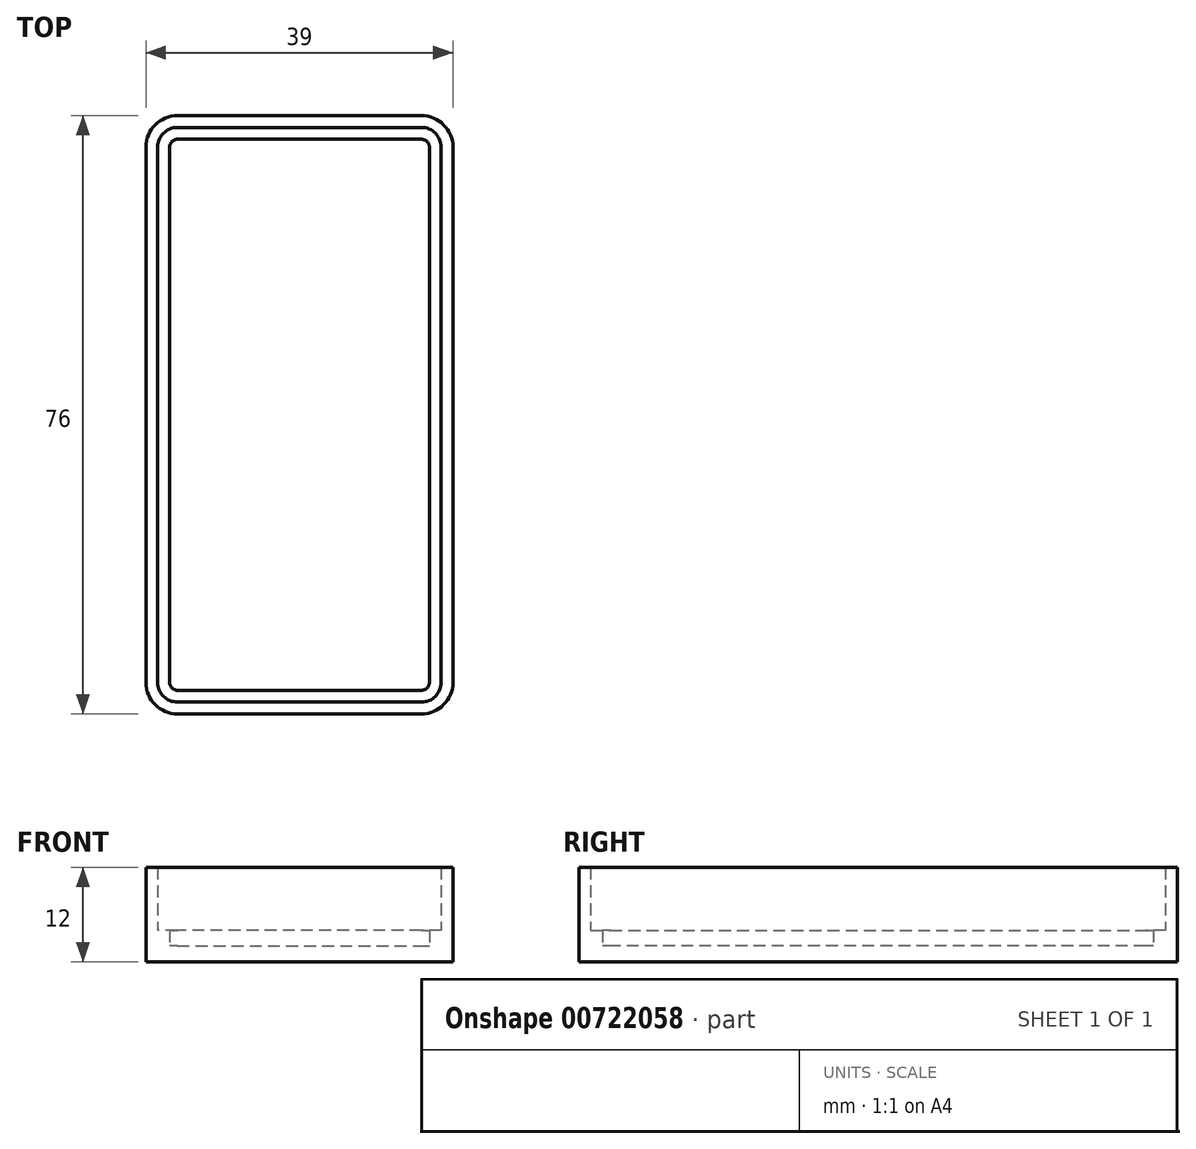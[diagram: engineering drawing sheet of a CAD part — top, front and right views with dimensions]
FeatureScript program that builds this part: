
annotation { "Feature Type Name" : "Feature", "Feature Type Description" : "" }
export const myFeature = defineFeature(function(context is Context, id is Id, definition is map)
    precondition{}
    {
        {
            var Q0;
            Q0=qCreatedBy(makeId("Top.planeOp"),FACE);
            var sketch = newSketch(context, id + "F0", { "sketchPlane" : qUnion([Q0])});
            skLineSegment(sketch, "E0.bottom", {"start": v(-15.5, 38) * mm, "end": v(15.5, 38) * mm});
            skLineSegment(sketch, "E0.top", {"start": v(-15.5, -38) * mm, "end": v(15.5, -38) * mm});
            skLineSegment(sketch, "E0.left", {"start": v(-19.5, 34) * mm, "end": v(-19.5, -34) * mm});
            skLineSegment(sketch, "E0.right", {"start": v(19.5, 34) * mm, "end": v(19.5, -34) * mm});
            skPoint(sketch, "E0.middle", {"position": v(0, 0) * mm});
            skPoint(sketch, "E1.visualSharp", {"position": v(-19.5, 38) * mm});
            skArc(sketch, "E1.filletArc", {"start": v(-15.5, 38) * mm, "mid": v(-18.33, 36.83) * mm, "end": v(-19.5, 34) * mm});
            skPoint(sketch, "E2.visualSharp", {"position": v(-19.5, -38) * mm});
            skArc(sketch, "E2.filletArc", {"start": v(-19.5, -34) * mm, "mid": v(-18.33, -36.83) * mm, "end": v(-15.5, -38) * mm});
            skPoint(sketch, "E3.visualSharp", {"position": v(19.5, -38) * mm});
            skArc(sketch, "E3.filletArc", {"start": v(15.5, -38) * mm, "mid": v(18.33, -36.83) * mm, "end": v(19.5, -34) * mm});
            skPoint(sketch, "E4.visualSharp", {"position": v(19.5, 38) * mm});
            skArc(sketch, "E4.filletArc", {"start": v(19.5, 34) * mm, "mid": v(18.33, 36.83) * mm, "end": v(15.5, 38) * mm});
            skSolve(sketch);
        }
        {
            var Q0;
            Q0 = qSketchRegion(id + "F0", true);
            extrude(context, id + "F1", {"entities" : qUnion([Q0]), "depth" : 2 * mm, "offsetDistance" : 25 * mm});
        }
        {
            var Q0;
            Q0=makeQuery(id+"F1.opExtrude","CAP_FACE",FACE,{"disambiguationData":[OSD([sQuery(id+"F0.wireOp",EDGE,"E0.bottom"),sQuery(id+"F0.wireOp",EDGE,"E0.top"),sQuery(id+"F0.wireOp",EDGE,"E0.left"),sQuery(id+"F0.wireOp",EDGE,"E0.right"),sQuery(id+"F0.wireOp",EDGE,"E1.filletArc"),sQuery(id+"F0.wireOp",EDGE,"E2.filletArc"),sQuery(id+"F0.wireOp",EDGE,"E3.filletArc"),sQuery(id+"F0.wireOp",EDGE,"E4.filletArc")])],"isStart":false});
            var sketch = newSketch(context, id + "F2", { "sketchPlane" : qUnion([Q0])});
            skLineSegment(sketch, "E5.0", {"start": v(19.5, 34) * mm, "end": v(19.5, -34) * mm});
            skArc(sketch, "E5.1", {"start": v(19.5, 34) * mm, "mid": v(18.33, 36.83) * mm, "end": v(15.5, 38) * mm});
            skLineSegment(sketch, "E5.2", {"start": v(-15.5, 38) * mm, "end": v(15.5, 38) * mm});
            skArc(sketch, "E5.3", {"start": v(-15.5, 38) * mm, "mid": v(-18.33, 36.83) * mm, "end": v(-19.5, 34) * mm});
            skLineSegment(sketch, "E5.4", {"start": v(-19.5, 34) * mm, "end": v(-19.5, -34) * mm});
            skArc(sketch, "E5.5", {"start": v(-19.5, -34) * mm, "mid": v(-18.33, -36.83) * mm, "end": v(-15.5, -38) * mm});
            skLineSegment(sketch, "E5.6", {"start": v(-15.5, -38) * mm, "end": v(15.5, -38) * mm});
            skArc(sketch, "E5.7", {"start": v(15.5, -38) * mm, "mid": v(18.33, -36.83) * mm, "end": v(19.5, -34) * mm});
            skArc(sketch, "E6.0", {"start": v(-15.5, 35) * mm, "mid": v(-16.2, 34.7) * mm, "end": v(-16.5, 34) * mm});
            skLineSegment(sketch, "E6.1", {"start": v(-16.5, 34) * mm, "end": v(-16.5, -34) * mm});
            skLineSegment(sketch, "E6.2", {"start": v(-15.5, 35) * mm, "end": v(15.5, 35) * mm});
            skArc(sketch, "E6.3", {"start": v(-16.5, -34) * mm, "mid": v(-16.2, -34.7) * mm, "end": v(-15.5, -35) * mm});
            skArc(sketch, "E6.4", {"start": v(16.5, 34) * mm, "mid": v(16.2, 34.7) * mm, "end": v(15.5, 35) * mm});
            skLineSegment(sketch, "E6.5", {"start": v(16.5, 34) * mm, "end": v(16.5, -34) * mm});
            skArc(sketch, "E6.6", {"start": v(15.5, -35) * mm, "mid": v(16.2, -34.7) * mm, "end": v(16.5, -34) * mm});
            skLineSegment(sketch, "E6.7", {"start": v(-15.5, -35) * mm, "end": v(15.5, -35) * mm});
            skSolve(sketch);
        }
        {
            var Q0;
            Q0 = qSketchRegion(id + "F2", true);
            extrude(context, id + "F3", {"entities" : qUnion([Q0]), "operationType" : NewBodyOperationType.ADD, "depth" : 2 * mm, "offsetDistance" : 25 * mm});
        }
        {
            var Q0;
            Q0=makeQuery(id+"F1.opExtrude","CAP_FACE",FACE,{"disambiguationData":[OSD([sQuery(id+"F0.wireOp",EDGE,"E0.bottom"),sQuery(id+"F0.wireOp",EDGE,"E0.top"),sQuery(id+"F0.wireOp",EDGE,"E0.left"),sQuery(id+"F0.wireOp",EDGE,"E0.right"),sQuery(id+"F0.wireOp",EDGE,"E1.filletArc"),sQuery(id+"F0.wireOp",EDGE,"E2.filletArc"),sQuery(id+"F0.wireOp",EDGE,"E3.filletArc"),sQuery(id+"F0.wireOp",EDGE,"E4.filletArc")])],"isStart":false});
            var sketch = newSketch(context, id + "F4", { "sketchPlane" : qUnion([Q0])});
            skLineSegment(sketch, "E7.0", {"start": v(-19.5, 34) * mm, "end": v(-19.5, -34) * mm});
            skArc(sketch, "E7.1", {"start": v(-15.5, 38) * mm, "mid": v(-18.33, 36.83) * mm, "end": v(-19.5, 34) * mm});
            skLineSegment(sketch, "E7.2", {"start": v(-15.5, 38) * mm, "end": v(15.5, 38) * mm});
            skArc(sketch, "E7.3", {"start": v(19.5, 34) * mm, "mid": v(18.33, 36.83) * mm, "end": v(15.5, 38) * mm});
            skLineSegment(sketch, "E7.4", {"start": v(19.5, 34) * mm, "end": v(19.5, -34) * mm});
            skArc(sketch, "E7.5", {"start": v(15.5, -38) * mm, "mid": v(18.33, -36.83) * mm, "end": v(19.5, -34) * mm});
            skLineSegment(sketch, "E7.6", {"start": v(-15.5, -38) * mm, "end": v(15.5, -38) * mm});
            skArc(sketch, "E7.7", {"start": v(-19.5, -34) * mm, "mid": v(-18.33, -36.83) * mm, "end": v(-15.5, -38) * mm});
            skArc(sketch, "E8.0", {"start": v(-15.5, 36.5) * mm, "mid": v(-17.27, 35.77) * mm, "end": v(-18, 34) * mm});
            skLineSegment(sketch, "E8.1", {"start": v(-15.5, 36.5) * mm, "end": v(15.5, 36.5) * mm});
            skLineSegment(sketch, "E8.2", {"start": v(-18, 34) * mm, "end": v(-18, -34) * mm});
            skArc(sketch, "E8.3", {"start": v(18, 34) * mm, "mid": v(17.27, 35.77) * mm, "end": v(15.5, 36.5) * mm});
            skArc(sketch, "E8.4", {"start": v(-18, -34) * mm, "mid": v(-17.27, -35.77) * mm, "end": v(-15.5, -36.5) * mm});
            skLineSegment(sketch, "E8.5", {"start": v(-15.5, -36.5) * mm, "end": v(15.5, -36.5) * mm});
            skArc(sketch, "E8.6", {"start": v(15.5, -36.5) * mm, "mid": v(17.27, -35.77) * mm, "end": v(18, -34) * mm});
            skLineSegment(sketch, "E8.7", {"start": v(18, 34) * mm, "end": v(18, -34) * mm});
            skSolve(sketch);
        }
        {
            var Q0;
            Q0 = qSketchRegion(id + "F4", true);
            extrude(context, id + "F5", {"entities" : qUnion([Q0]), "operationType" : NewBodyOperationType.ADD, "depth" : 10 * mm, "offsetDistance" : 25 * mm});
        }
    });
